# Revit family: MarshallTufflex_ElectricalFittings_TrunkingDado_Mini_MMT5a
name_source: partatom
category: Generic Models
revit_build: Autodesk Revit 2016 (Build: 20150714_1515(x64)
units: mm (PartAtom-declared; Revit-internal decimal feet)

## family parameters
Can host rebar = No
Cut with Voids When Loaded = Yes
Host = Face
OmniClass Number = 23.80.30.17.14
OmniClass Title = Wireways
Part Type = Normal
Room Calculation Point = No
Round Connector Dimension = Use Diameter
Shared = Yes

## types (1)
- MMT5
    AccessClearanceBottom = 0 mm  [stored 0 ft]
    AccessClearanceFront = 0 mm  [stored 0 ft]
    AccessClearanceLeft = 0 mm  [stored 0 ft]
    AccessClearanceRear = 0 mm  [stored 0 ft]
    AccessClearanceRight = 0 mm  [stored 0 ft]
    AccessClearanceTop = 0 mm  [stored 0 ft]
    Accessories = www.marshall-tufflex.com
    Assembly Code = D5010
    AssetType = Fixed
    BIMObjectName = MarshallTufflex_ElectricalFittings_TrunkingDado_Mini_MMT5
    CEApproval = Yes
    ClassificationName = Uniclass2015
    ClassificationValue = Pr_65_70_11_61
    Color = White (RAL9003)
    Colour = White (RAL9003)
    Compartments = No
    Constituents = Mini Trunking
    Cost = 0 $
    Default Elevation = 1200 mm
    Description = Trunking Dado MT Mini MMT5
    DocumentationCertificates = www.marshall-tufflex.com
    DocumentationInstallationGuide = www.marshall-tufflex.com
    DocumentationLiterature = www.marshall-tufflex.com
    DocumentationMaintenance = www.marshall-tufflex.com
    DocumentationTechnical = www.marshall-tufflex.com
    DurationUnit = Years
    EmbodiedCarbon = 0
    EnclosureRating = IP4X
    ExpectedLife = 0
    Features = Variety of sizes, self-fixing and punched options
    Finish = Matt
    Fittings = www.marshall-tufflex.com
    GreenGuideforSpecification = 0
    GrossWeight = 0
    IfcExportAs = IfcFlowSegment
    IfcExportType = IfcCableSegmentType
    Keynote = V90
    LidConfiguration = Tamper Proof
    LocationOfManufacturer = N 50°52'39" E 0°31'41"
    Manufacturer = Marshall-Tufflex Ltd
    ManufacturerName = Marshall-Tufflex Ltd
    ManufacturerWebsite = www.marshall-tufflex.com
    Material = PVCu
    Model = Mini
    ModelNumber = MMT5
    ModelReference = Mini
    NBSDescription = Proprietry Tunking
    NBSObjectName = MT MiniTrunkingMMT5
    NBSReference = 90-55-10/390
    NominalDepth = 25 mm  [stored 0.082021 ft]
    NominalHeight = 50 mm  [stored 0.164042 ft]
    NominalLength = 3000 mm  [stored 9.84252 ft]
    O&Mmanual = www.marshall-tufflex.com
    OverallHeight = 50 mm  [stored 0.164042 ft]
    OverallWidth = 25 mm  [stored 0.082021 ft]
    ProductLiterature = www.marshall-tufflex.com
    ProductModelNumber = MMT5
    ProductRange = Mini
    ProductionYear = 2018
    ReferenceStandard = BS EN 50085-1
    ReferencedStandard = BS EN 50085-1
    Shape = 50x25mm
    ShippingWeight = 0
    Sub-Type = Dado
    Type = Trunking
    Type Comments = Dado Trunking Single Compartment With Cover
    TypeName = Marshall Tufflex Electrical Fitting Trunking Dado Mini
    URL = www.marshall-tufflex.com
    WarrantyDurationLabor = 0
    WarrantyDurationParts = 0
    WarrantyDurationUnit = Years
    _BSBibleVersion = 15
    _BimSpecGuid = 0
    _CurrentRevision = 1
    _DistributedBy = www.bimstore.co.uk

note: [stored X ft] marks values corroborated as IEEE doubles in the binary element streams (Revit-internal decimal feet)

## geometry (parser evidence)
native form markers: Blend x2, Sweep x17
no freeform markers — native parametric forms only
